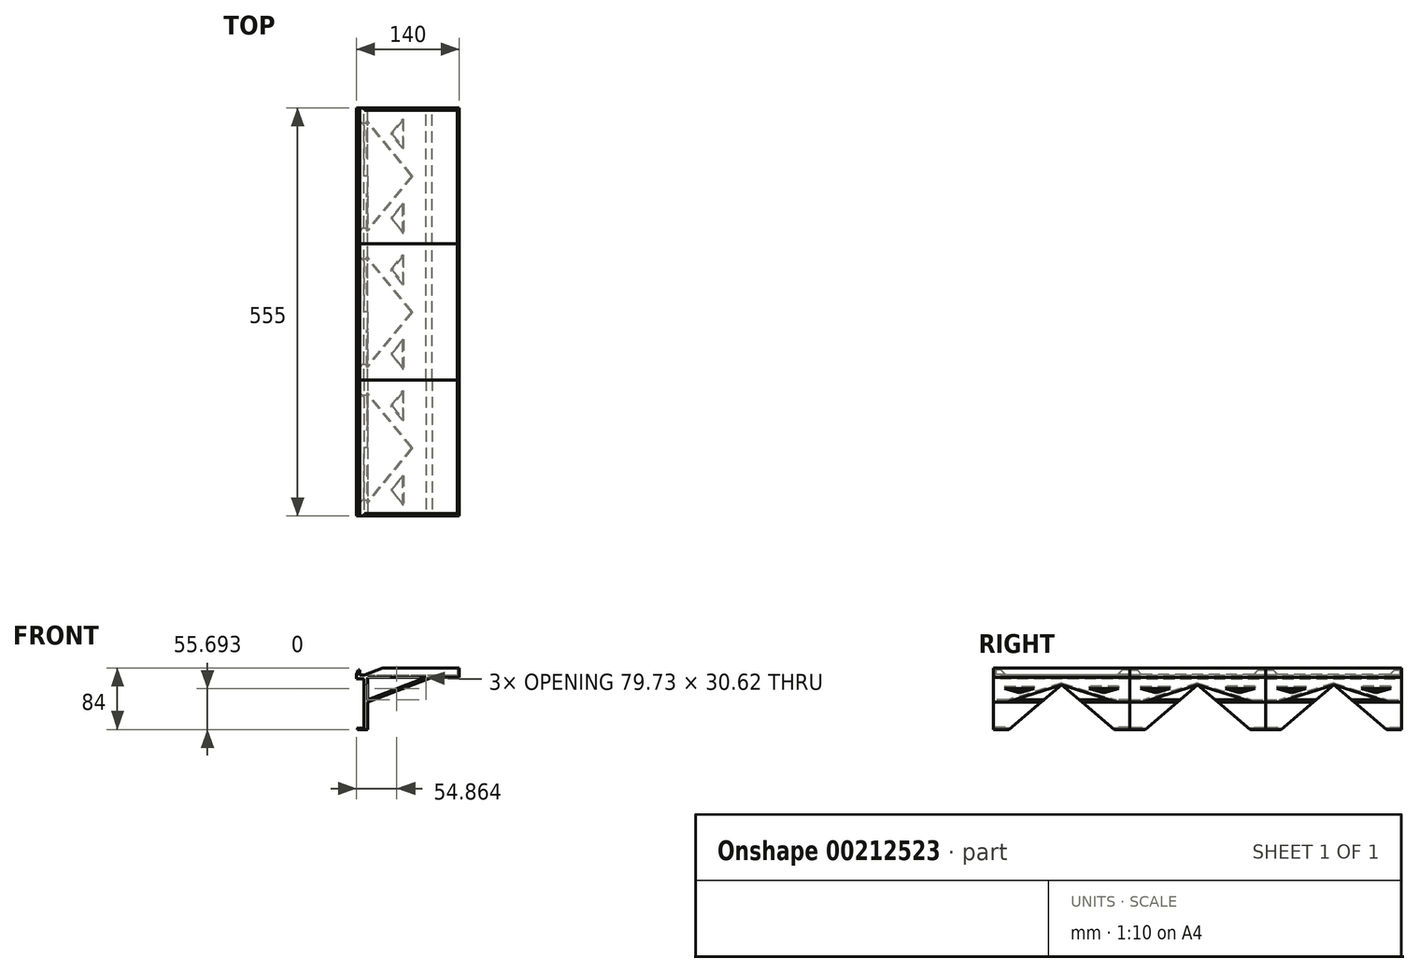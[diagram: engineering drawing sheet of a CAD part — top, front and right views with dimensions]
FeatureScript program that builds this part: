
annotation { "Feature Type Name" : "Feature", "Feature Type Description" : "" }
export const myFeature = defineFeature(function(context is Context, id is Id, definition is map)
    precondition{}
    {
        {
            var Q0;
            Q0=qCreatedBy(makeId("Front.planeOp"),FACE);
            var sketch = newSketch(context, id + "F0", { "sketchPlane" : qUnion([Q0])});
            skLineSegment(sketch, "E0", {"start": v(4.72, -35.17) * mm, "end": v(4.72, 31.83) * mm});
            skLineSegment(sketch, "E1", {"start": v(4.72, 31.83) * mm, "end": v(-5.28, 31.83) * mm});
            skLineSegment(sketch, "E2", {"start": v(-5.28, 31.83) * mm, "end": v(-5.28, 37.83) * mm});
            skLineSegment(sketch, "E3", {"start": v(-3.03, 43.83) * mm, "end": v(-0.78, 43.83) * mm});
            skLineSegment(sketch, "E4", {"start": v(-0.78, 43.83) * mm, "end": v(-0.78, 36.83) * mm});
            skLineSegment(sketch, "E5", {"start": v(-0.78, 36.83) * mm, "end": v(9.72, 36.83) * mm});
            skLineSegment(sketch, "E6", {"start": v(9.72, 33.83) * mm, "end": v(9.72, 3.21) * mm});
            skLineSegment(sketch, "E7", {"start": v(9.72, -37.17) * mm, "end": v(-3.78, -37.17) * mm});
            skLineSegment(sketch, "E8", {"start": v(-3.78, -37.17) * mm, "end": v(-3.78, -35.17) * mm});
            skLineSegment(sketch, "E9", {"start": v(-0.78, -35.17) * mm, "end": v(4.72, -35.17) * mm});
            skLineSegment(sketch, "E10", {"start": v(9.72, 36.83) * mm, "end": v(131.72, 36.83) * mm});
            skLineSegment(sketch, "E11", {"start": v(134.72, 36.83) * mm, "end": v(134.72, 33.83) * mm});
            skLineSegment(sketch, "E12", {"start": v(134.72, 33.83) * mm, "end": v(97.82, 33.83) * mm});
            skLineSegment(sketch, "E13", {"start": v(-3.03, 43.83) * mm, "end": v(-5.28, 37.83) * mm});
            skPoint(sketch, "E14.orphan", {"position": v(-5.28, 43.83) * mm});
            skLineSegment(sketch, "E15", {"start": v(-0.78, -35.17) * mm, "end": v(-2.28, -34.42) * mm});
            skLineSegment(sketch, "E16", {"start": v(-2.28, -34.42) * mm, "end": v(-3.78, -35.17) * mm});
            skLineSegment(sketch, "E17", {"start": v(134.72, 36.83) * mm, "end": v(134.72, 46.83) * mm});
            skLineSegment(sketch, "E18", {"start": v(134.72, 46.83) * mm, "end": v(131.72, 46.83) * mm});
            skLineSegment(sketch, "E19", {"start": v(131.72, 46.83) * mm, "end": v(131.72, 36.83) * mm});
            skLineSegment(sketch, "E20", {"start": v(9.72, 0) * mm, "end": v(97.82, 33.83) * mm});
            skLineSegment(sketch, "E21.0", {"start": v(9.72, 3.21) * mm, "end": v(89.45, 33.83) * mm});
            skLineSegment(sketch, "E22.trimOffspring", {"start": v(9.72, 0) * mm, "end": v(9.72, -37.17) * mm});
            skLineSegment(sketch, "E23.trimOffspring", {"start": v(89.45, 33.83) * mm, "end": v(9.72, 33.83) * mm});
            skSolve(sketch);
        }
        {
            var Q0;
            Q0=makeQuery(id+"F0.imprint","IMPRINT",FACE,{"disambiguationData":[TD([[makeQuery(id+"F0.imprint","IMPRINT",EDGE,{"derivedFrom":sQuery(id+"F0.wireOp",EDGE,"E0")}),-1.0]])]});
            extrude(context, id + "F1", {"entities" : qUnion([Q0]), "endBound" : BoundingType.SYMMETRIC, "depth" : 185 * mm, "offsetDistance" : 25 * mm});
        }
        {
            var Q0;
            Q0=makeQuery(id+"F1.opExtrude","SWEPT_FACE",FACE,{"disambiguationData":[OSD([sQuery(id+"F0.wireOp",EDGE,"E4")])]});
            var sketch = newSketch(context, id + "F2", { "sketchPlane" : qUnion([Q0])});
            skLineSegment(sketch, "E24", {"start": v(-92.5, 43.83) * mm, "end": v(-82.5, 43.83) * mm, "construction": true});
            skLineSegment(sketch, "E25", {"start": v(-82.5, 43.83) * mm, "end": v(-76.17, 37.5) * mm});
            skLineSegment(sketch, "E26.MirrorCS", {"start": v(82.5, 43.83) * mm, "end": v(76.17, 37.5) * mm});
            skLineSegment(sketch, "E27", {"start": v(-76.17, 37.5) * mm, "end": v(76.17, 37.5) * mm});
            skLineSegment(sketch, "E28", {"start": v(-82.5, 43.83) * mm, "end": v(82.5, 43.83) * mm});
            skSolve(sketch);
        }
        {
            var Q0;
            Q0=makeQuery(id+"F2.imprint","IMPRINT",FACE,{"disambiguationData":[TD([[makeQuery(id+"F2.imprint","IMPRINT",EDGE,{"derivedFrom":sQuery(id+"F2.wireOp",EDGE,"E25")}),1.0]])]});
            extrude(context, id + "F3", {"entities" : qUnion([Q0]), "operationType" : NewBodyOperationType.REMOVE, "endBound" : BoundingType.THROUGH_ALL, "oppositeDirection" : true, "depth" : 25 * mm, "offsetDistance" : 25 * mm});
        }
        {
            var Q0;
            Q0=qCreatedBy(makeId("Front.planeOp"),FACE);
            cPlane(context, id + "F4", {"entities" : qUnion([Q0]), "cplaneType" : CPlaneType.OFFSET, "offset" : 92.5 * mm, "width" : 150 * mm, "height" : 150 * mm});
        }
        {
            var Q0;
            Q0=makeQuery(id+"F1.opExtrude","SWEPT_FACE",FACE,{"disambiguationData":[OSD([sQuery(id+"F0.wireOp",EDGE,"E0")])]});
            var sketch = newSketch(context, id + "F5", { "sketchPlane" : qUnion([Q0])});
            skLineSegment(sketch, "E29", {"start": v(-86.31, -49.69) * mm, "end": v(0, 23.55) * mm});
            skPoint(sketch, "E29.endSnap0", {"position": v(0, 31.83) * mm});
            skLineSegment(sketch, "E30.MirrorCS", {"start": v(86.31, -49.69) * mm, "end": v(0, 23.55) * mm});
            skLineSegment(sketch, "E31", {"start": v(-86.31, -49.69) * mm, "end": v(86.31, -49.69) * mm});
            skLineSegment(sketch, "E32.MirrorCS", {"start": v(98.69, -49.69) * mm, "end": v(185, 23.55) * mm});
            skLineSegment(sketch, "E33.MirrorCS", {"start": v(271.31, -49.69) * mm, "end": v(185, 23.55) * mm});
            skLineSegment(sketch, "E34.MirrorCS", {"start": v(271.31, -49.69) * mm, "end": v(98.69, -49.69) * mm});
            skLineSegment(sketch, "E35.MirrorCS", {"start": v(-98.69, -49.69) * mm, "end": v(-185, 23.55) * mm});
            skLineSegment(sketch, "E36.MirrorCS", {"start": v(-271.31, -49.69) * mm, "end": v(-185, 23.55) * mm});
            skLineSegment(sketch, "E37.MirrorCS", {"start": v(-271.31, -49.69) * mm, "end": v(-98.69, -49.69) * mm});
            skSolve(sketch);
        }
        {
            var Q0;
            Q0=makeQuery(id+"F5.imprint","IMPRINT",FACE,{"disambiguationData":[TD([[makeQuery(id+"F5.imprint","IMPRINT",EDGE,{"derivedFrom":sQuery(id+"F5.wireOp",EDGE,"E35.MirrorCS")}),1.0]])]});
            var Q1;
            {var subQ0=sQuery(id+"F5.wireOp",EDGE,"E30.MirrorCS");var subQ1=sQuery(id+"F5.wireOp",EDGE,"E29");var subQ2=makeQuery(id+"F5.imprint","INTERSECT",VERTEX,{"derivedFrom":[subQ1,subQ0]});Q1=makeQuery(id+"F5.imprint","IMPRINT",FACE,{"disambiguationData":[TD([[makeQuery(id+"F5.imprint","IMPRINT",EDGE,{"disambiguationData":[TD([[subQ2,1.0]])],"derivedFrom":subQ1}),-1.0]])]});}
            var Q2;
            {var subQ0=sQuery(id+"F5.wireOp",EDGE,"E31");Q2=makeQuery(id+"F5.imprint","IMPRINT",FACE,{"disambiguationData":[TD([[makeQuery(id+"F5.imprint","IMPRINT",EDGE,{"derivedFrom":subQ0}),1.0]])]});}
            var Q3;
            Q3=makeQuery(id+"F5.imprint","IMPRINT",FACE,{"disambiguationData":[TD([[makeQuery(id+"F5.imprint","IMPRINT",EDGE,{"derivedFrom":sQuery(id+"F5.wireOp",EDGE,"E32.MirrorCS")}),-1.0]])]});
            extrude(context, id + "F6", {"entities" : qUnion([Q0, Q1, Q2, Q3]), "operationType" : NewBodyOperationType.REMOVE, "endBound" : BoundingType.THROUGH_ALL, "oppositeDirection" : true, "depth" : 25 * mm, "offsetDistance" : 25 * mm});
        }
        {
            var Q0;
            Q0=makeQuery(id+"F1.opExtrude","SWEPT_FACE",FACE,{"disambiguationData":[OSD([sQuery(id+"F0.wireOp",EDGE,"E0")])]});
            var sketch = newSketch(context, id + "F7", { "sketchPlane" : qUnion([Q0])});
            skLineSegment(sketch, "E38", {"start": v(-67.86, -34.04) * mm, "end": v(-71.94, -37.5) * mm});
            skLineSegment(sketch, "E39", {"start": v(-67.86, -34.04) * mm, "end": v(67.86, -34.04) * mm});
            skLineSegment(sketch, "E40", {"start": v(67.86, -34.04) * mm, "end": v(71.94, -37.5) * mm});
            skLineSegment(sketch, "E41", {"start": v(-71.94, -37.5) * mm, "end": v(71.94, -37.5) * mm});
            skLineSegment(sketch, "E42.MirrorCS", {"start": v(252.86, -34.04) * mm, "end": v(256.94, -37.5) * mm});
            skLineSegment(sketch, "E43.MirrorCS", {"start": v(117.14, -34.04) * mm, "end": v(113.06, -37.5) * mm});
            skLineSegment(sketch, "E44.MirrorCS", {"start": v(256.94, -37.5) * mm, "end": v(113.06, -37.5) * mm});
            skLineSegment(sketch, "E45.MirrorCS", {"start": v(252.86, -34.04) * mm, "end": v(117.14, -34.04) * mm});
            skSolve(sketch);
        }
        {
            var Q0;
            {var subQ32=sQuery(id+"F7.wireOp",EDGE,"E39");Q0=makeQuery(id+"F7.imprint","IMPRINT",FACE,{"disambiguationData":[TD([[makeQuery(id+"F7.imprint","IMPRINT",EDGE,{"derivedFrom":subQ32}),-1.0]])]});}
            var Q1;
            Q1=makeQuery(id+"F7.imprint","IMPRINT",FACE,{"disambiguationData":[TD([[makeQuery(id+"F7.imprint","IMPRINT",EDGE,{"derivedFrom":sQuery(id+"F7.wireOp",EDGE,"E42.MirrorCS")}),-1.0]])]});
            extrude(context, id + "F8", {"entities" : qUnion([Q0, Q1]), "operationType" : NewBodyOperationType.REMOVE, "endBound" : BoundingType.THROUGH_ALL, "depth" : 25 * mm, "offsetDistance" : 25 * mm});
        }
        {
            var Q0;
            Q0=makeQuery(id+"F1.opExtrude","SWEPT_FACE",FACE,{"disambiguationData":[OSD([sQuery(id+"F0.wireOp",EDGE,"E20")])]});
            var sketch = newSketch(context, id + "F9", { "sketchPlane" : qUnion([Q0])});
            skLineSegment(sketch, "E46", {"start": v(74.75, 0) * mm, "end": v(9.07, 74.66) * mm});
            skLineSegment(sketch, "E47.MirrorCS", {"start": v(74.75, 0) * mm, "end": v(9.07, -74.66) * mm});
            skLineSegment(sketch, "E48", {"start": v(9.07, 74.66) * mm, "end": v(9.07, -74.66) * mm});
            skSolve(sketch);
        }
        {
            var Q0;
            {var subQ0=sQuery(id+"F9.wireOp",EDGE,"E46");Q0=makeQuery(id+"F9.imprint","IMPRINT",FACE,{"disambiguationData":[TD([[makeQuery(id+"F9.imprint","IMPRINT",EDGE,{"derivedFrom":subQ0}),1.0]])]});}
            var Q1;
            {var subQ1=makeQuery(id+"F1.opExtrude","SWEPT_FACE",FACE,{"disambiguationData":[OSD([sQuery(id+"F0.wireOp",EDGE,"E20")])]});var subQ2=makeQuery(id+"F6.boolean.opBoolean","INTERSECT",EDGE,{"derivedFrom":[subQ1,makeQuery(id+"F6.opExtrude","SWEPT_FACE",FACE,{"disambiguationData":[OSD([sQuery(id+"F5.wireOp",EDGE,"E29")])]})]});Q1=makeQuery(id+"F9.imprint","IMPRINT",FACE,{"disambiguationData":[TD([[makeQuery(id+"F9.imprint","IMPRINT",EDGE,{"derivedFrom":subQ2}),1.0]])]});}
            var Q2;
            {var subQ0=sQuery(id+"F9.wireOp",EDGE,"E47.MirrorCS");Q2=makeQuery(id+"F9.imprint","IMPRINT",FACE,{"disambiguationData":[TD([[makeQuery(id+"F9.imprint","IMPRINT",EDGE,{"derivedFrom":subQ0}),-1.0]])]});}
            extrude(context, id + "F10", {"entities" : qUnion([Q0, Q1, Q2]), "operationType" : NewBodyOperationType.REMOVE, "oppositeDirection" : true, "depth" : 3 * mm, "offsetDistance" : 25 * mm});
        }
        {
            var Q0;
            Q0=makeQuery(id+"F1.opExtrude","SWEPT_BODY",BODY,{"disambiguationData":[OSD([sQuery(id+"F0.wireOp",EDGE,"E0"),sQuery(id+"F0.wireOp",EDGE,"E1"),sQuery(id+"F0.wireOp",EDGE,"E2"),sQuery(id+"F0.wireOp",EDGE,"E3"),sQuery(id+"F0.wireOp",EDGE,"E4"),sQuery(id+"F0.wireOp",EDGE,"E5"),sQuery(id+"F0.wireOp",EDGE,"E6"),sQuery(id+"F0.wireOp",EDGE,"E7"),sQuery(id+"F0.wireOp",EDGE,"E8"),sQuery(id+"F0.wireOp",EDGE,"E9"),sQuery(id+"F0.wireOp",EDGE,"E10"),sQuery(id+"F0.wireOp",EDGE,"E11"),sQuery(id+"F0.wireOp",EDGE,"E12"),sQuery(id+"F0.wireOp",EDGE,"E13"),sQuery(id+"F0.wireOp",EDGE,"E15"),sQuery(id+"F0.wireOp",EDGE,"E16"),sQuery(id+"F0.wireOp",EDGE,"E17"),sQuery(id+"F0.wireOp",EDGE,"E18"),sQuery(id+"F0.wireOp",EDGE,"E19"),sQuery(id+"F0.wireOp",EDGE,"E20"),sQuery(id+"F0.wireOp",EDGE,"E21.0"),sQuery(id+"F0.wireOp",EDGE,"E22.trimOffspring"),sQuery(id+"F0.wireOp",EDGE,"E23.trimOffspring")])]});
            var Q1;
            Q1=qCreatedBy(id+"F4.planeOp",FACE);
            mirror(context, id + "F11", {"entities" : qUnion([Q0]), "mirrorPlane" : qUnion([Q1])});
        }
        {
            var Q0;
            Q0=makeQuery(id+"F11.opPattern","COPY",FACE,{"derivedFrom":makeQuery(id+"F1.opExtrude","CAP_FACE",FACE,{"disambiguationData":[OSD([sQuery(id+"F0.wireOp",EDGE,"E0"),sQuery(id+"F0.wireOp",EDGE,"E1"),sQuery(id+"F0.wireOp",EDGE,"E2"),sQuery(id+"F0.wireOp",EDGE,"E3"),sQuery(id+"F0.wireOp",EDGE,"E4"),sQuery(id+"F0.wireOp",EDGE,"E5"),sQuery(id+"F0.wireOp",EDGE,"E6"),sQuery(id+"F0.wireOp",EDGE,"E7"),sQuery(id+"F0.wireOp",EDGE,"E8"),sQuery(id+"F0.wireOp",EDGE,"E9"),sQuery(id+"F0.wireOp",EDGE,"E10"),sQuery(id+"F0.wireOp",EDGE,"E11"),sQuery(id+"F0.wireOp",EDGE,"E12"),sQuery(id+"F0.wireOp",EDGE,"E13"),sQuery(id+"F0.wireOp",EDGE,"E15"),sQuery(id+"F0.wireOp",EDGE,"E16"),sQuery(id+"F0.wireOp",EDGE,"E17"),sQuery(id+"F0.wireOp",EDGE,"E18"),sQuery(id+"F0.wireOp",EDGE,"E19"),sQuery(id+"F0.wireOp",EDGE,"E20"),sQuery(id+"F0.wireOp",EDGE,"E21.0"),sQuery(id+"F0.wireOp",EDGE,"E22.trimOffspring"),sQuery(id+"F0.wireOp",EDGE,"E23.trimOffspring")])],"isStart":true}),"instanceName":"1"});
            var sketch = newSketch(context, id + "F12", { "sketchPlane" : qUnion([Q0])});
            skLineSegment(sketch, "E49", {"start": v(5.8, 36.83) * mm, "end": v(131.72, 36.83) * mm});
            skLineSegment(sketch, "E50", {"start": v(131.72, 36.83) * mm, "end": v(131.72, 46.83) * mm});
            skLineSegment(sketch, "E51", {"start": v(131.72, 46.83) * mm, "end": v(24.2, 46.83) * mm});
            skLineSegment(sketch, "E52", {"start": v(24.2, 46.83) * mm, "end": v(5.8, 36.83) * mm});
            skSolve(sketch);
        }
        {
            var Q0;
            Q0=makeQuery(id+"F12.imprint","IMPRINT",FACE,{"disambiguationData":[TD([[makeQuery(id+"F12.imprint","IMPRINT",EDGE,{"derivedFrom":sQuery(id+"F12.wireOp",EDGE,"E49")}),1.0]])]});
            extrude(context, id + "F13", {"entities" : qUnion([Q0]), "operationType" : NewBodyOperationType.ADD, "oppositeDirection" : true, "depth" : 3 * mm, "offsetDistance" : 25 * mm});
        }
        {
            var Q0;
            Q0=makeQuery(id+"F11.opPattern","COPY",BODY,{"derivedFrom":makeQuery(id+"F1.opExtrude","SWEPT_BODY",BODY,{"disambiguationData":[OSD([sQuery(id+"F0.wireOp",EDGE,"E0"),sQuery(id+"F0.wireOp",EDGE,"E1"),sQuery(id+"F0.wireOp",EDGE,"E2"),sQuery(id+"F0.wireOp",EDGE,"E3"),sQuery(id+"F0.wireOp",EDGE,"E4"),sQuery(id+"F0.wireOp",EDGE,"E5"),sQuery(id+"F0.wireOp",EDGE,"E6"),sQuery(id+"F0.wireOp",EDGE,"E7"),sQuery(id+"F0.wireOp",EDGE,"E8"),sQuery(id+"F0.wireOp",EDGE,"E9"),sQuery(id+"F0.wireOp",EDGE,"E10"),sQuery(id+"F0.wireOp",EDGE,"E11"),sQuery(id+"F0.wireOp",EDGE,"E12"),sQuery(id+"F0.wireOp",EDGE,"E13"),sQuery(id+"F0.wireOp",EDGE,"E15"),sQuery(id+"F0.wireOp",EDGE,"E16"),sQuery(id+"F0.wireOp",EDGE,"E17"),sQuery(id+"F0.wireOp",EDGE,"E18"),sQuery(id+"F0.wireOp",EDGE,"E19"),sQuery(id+"F0.wireOp",EDGE,"E20"),sQuery(id+"F0.wireOp",EDGE,"E21.0"),sQuery(id+"F0.wireOp",EDGE,"E22.trimOffspring"),sQuery(id+"F0.wireOp",EDGE,"E23.trimOffspring")])]}),"instanceName":"1"});
            var Q1;
            Q1=qCreatedBy(makeId("Front.planeOp"),FACE);
            mirror(context, id + "F14", {"entities" : qUnion([Q0]), "mirrorPlane" : qUnion([Q1])});
        }
        {
            var Q0;
            {var subQ2=sQuery(id+"F0.wireOp",EDGE,"E7");Q0=makeQuery(id+"F8.boolean.opBoolean","SPLIT",FACE,{"disambiguationData":[TD([makeQuery(id+"F6.boolean.opBoolean","COPY",FACE,{"derivedFrom":makeQuery(id+"F6.opExtrude","SWEPT_FACE",FACE,{"disambiguationData":[OSD([sQuery(id+"F5.wireOp",EDGE,"E30.MirrorCS")])]})})])],"derivedFrom":makeQuery(id+"F1.opExtrude","SWEPT_FACE",FACE,{"disambiguationData":[OSD([subQ2])]})});}
            var sketch = newSketch(context, id + "F15", { "sketchPlane" : qUnion([Q0])});
            skLineSegment(sketch, "E53", {"start": v(4.66, 69.27) * mm, "end": v(-3.78, 78.71) * mm});
            skLineSegment(sketch, "E54", {"start": v(-3.78, 78.71) * mm, "end": v(-3.78, 67.84) * mm});
            skLineSegment(sketch, "E55", {"start": v(-3.78, 67.84) * mm, "end": v(4.66, 69.27) * mm});
            skLineSegment(sketch, "E56.MirrorCS", {"start": v(4.66, -69.27) * mm, "end": v(-3.78, -78.71) * mm});
            skLineSegment(sketch, "E57.MirrorCS", {"start": v(-3.78, -78.71) * mm, "end": v(-3.78, -67.84) * mm});
            skLineSegment(sketch, "E58.MirrorCS", {"start": v(-3.78, -67.84) * mm, "end": v(4.66, -69.27) * mm});
            skSolve(sketch);
        }
        {
            var Q0;
            {var subQ0=sQuery(id+"F15.wireOp",EDGE,"E55");Q0=makeQuery(id+"F15.imprint","IMPRINT",FACE,{"disambiguationData":[TD([[makeQuery(id+"F15.imprint","IMPRINT",EDGE,{"derivedFrom":subQ0}),1.0]])]});}
            var Q1;
            {var subQ0=sQuery(id+"F15.wireOp",EDGE,"E54");var subQ3=sQuery(id+"F0.wireOp",EDGE,"E7");var subQ4=makeQuery(id+"F1.opExtrude","SWEPT_FACE",FACE,{"disambiguationData":[OSD([subQ3])]});var subQ5=makeQuery(id+"F8.opExtrude","SWEPT_FACE",FACE,{"disambiguationData":[OSD([sQuery(id+"F7.wireOp",EDGE,"E40")])]});var subQ7=makeQuery(id+"F8.boolean.opBoolean","INTERSECT",EDGE,{"derivedFrom":[subQ4,subQ5]});var subQ9=makeQuery(id+"F15.imprint","INTERSECT",VERTEX,{"derivedFrom":[subQ7,subQ0]});Q1=makeQuery(id+"F15.imprint","IMPRINT",FACE,{"disambiguationData":[TD([[makeQuery(id+"F15.imprint","IMPRINT",EDGE,{"disambiguationData":[TD([[subQ9,1.0]])],"derivedFrom":subQ7}),-1.0]])]});}
            var Q2;
            Q2=makeQuery(id+"F15.imprint","IMPRINT",FACE,{"disambiguationData":[TD([[makeQuery(id+"F15.imprint","IMPRINT",EDGE,{"derivedFrom":sQuery(id+"F15.wireOp",EDGE,"E56.MirrorCS")}),-1.0]])]});
            extrude(context, id + "F16", {"entities" : qUnion([Q0, Q1, Q2]), "operationType" : NewBodyOperationType.REMOVE, "oppositeDirection" : true, "depth" : 6 * mm, "offsetDistance" : 25 * mm});
        }
        {
            var Q0;
            Q0=makeQuery(id+"F14.opPattern","COPY",BODY,{"derivedFrom":makeQuery(id+"F11.opPattern","COPY",BODY,{"derivedFrom":makeQuery(id+"F1.opExtrude","SWEPT_BODY",BODY,{"disambiguationData":[OSD([sQuery(id+"F0.wireOp",EDGE,"E0"),sQuery(id+"F0.wireOp",EDGE,"E1"),sQuery(id+"F0.wireOp",EDGE,"E2"),sQuery(id+"F0.wireOp",EDGE,"E3"),sQuery(id+"F0.wireOp",EDGE,"E4"),sQuery(id+"F0.wireOp",EDGE,"E5"),sQuery(id+"F0.wireOp",EDGE,"E6"),sQuery(id+"F0.wireOp",EDGE,"E7"),sQuery(id+"F0.wireOp",EDGE,"E8"),sQuery(id+"F0.wireOp",EDGE,"E9"),sQuery(id+"F0.wireOp",EDGE,"E10"),sQuery(id+"F0.wireOp",EDGE,"E11"),sQuery(id+"F0.wireOp",EDGE,"E12"),sQuery(id+"F0.wireOp",EDGE,"E13"),sQuery(id+"F0.wireOp",EDGE,"E15"),sQuery(id+"F0.wireOp",EDGE,"E16"),sQuery(id+"F0.wireOp",EDGE,"E17"),sQuery(id+"F0.wireOp",EDGE,"E18"),sQuery(id+"F0.wireOp",EDGE,"E19"),sQuery(id+"F0.wireOp",EDGE,"E20"),sQuery(id+"F0.wireOp",EDGE,"E21.0"),sQuery(id+"F0.wireOp",EDGE,"E22.trimOffspring"),sQuery(id+"F0.wireOp",EDGE,"E23.trimOffspring")])]}),"instanceName":"1"}),"instanceName":"1"});
            deleteBodies(context, id + "F17", {"entities" : qUnion([Q0])});
        }
        {
            var Q0;
            Q0=makeQuery(id+"F11.opPattern","COPY",BODY,{"derivedFrom":makeQuery(id+"F1.opExtrude","SWEPT_BODY",BODY,{"disambiguationData":[OSD([sQuery(id+"F0.wireOp",EDGE,"E0"),sQuery(id+"F0.wireOp",EDGE,"E1"),sQuery(id+"F0.wireOp",EDGE,"E2"),sQuery(id+"F0.wireOp",EDGE,"E3"),sQuery(id+"F0.wireOp",EDGE,"E4"),sQuery(id+"F0.wireOp",EDGE,"E5"),sQuery(id+"F0.wireOp",EDGE,"E6"),sQuery(id+"F0.wireOp",EDGE,"E7"),sQuery(id+"F0.wireOp",EDGE,"E8"),sQuery(id+"F0.wireOp",EDGE,"E9"),sQuery(id+"F0.wireOp",EDGE,"E10"),sQuery(id+"F0.wireOp",EDGE,"E11"),sQuery(id+"F0.wireOp",EDGE,"E12"),sQuery(id+"F0.wireOp",EDGE,"E13"),sQuery(id+"F0.wireOp",EDGE,"E15"),sQuery(id+"F0.wireOp",EDGE,"E16"),sQuery(id+"F0.wireOp",EDGE,"E17"),sQuery(id+"F0.wireOp",EDGE,"E18"),sQuery(id+"F0.wireOp",EDGE,"E19"),sQuery(id+"F0.wireOp",EDGE,"E20"),sQuery(id+"F0.wireOp",EDGE,"E21.0"),sQuery(id+"F0.wireOp",EDGE,"E22.trimOffspring"),sQuery(id+"F0.wireOp",EDGE,"E23.trimOffspring")])]}),"instanceName":"1"});
            deleteBodies(context, id + "F18", {"entities" : qUnion([Q0])});
        }
        {
            var Q0;
            Q0=makeQuery(id+"F1.opExtrude","SWEPT_BODY",BODY,{"disambiguationData":[OSD([sQuery(id+"F0.wireOp",EDGE,"E0"),sQuery(id+"F0.wireOp",EDGE,"E1"),sQuery(id+"F0.wireOp",EDGE,"E2"),sQuery(id+"F0.wireOp",EDGE,"E3"),sQuery(id+"F0.wireOp",EDGE,"E4"),sQuery(id+"F0.wireOp",EDGE,"E5"),sQuery(id+"F0.wireOp",EDGE,"E6"),sQuery(id+"F0.wireOp",EDGE,"E7"),sQuery(id+"F0.wireOp",EDGE,"E8"),sQuery(id+"F0.wireOp",EDGE,"E9"),sQuery(id+"F0.wireOp",EDGE,"E10"),sQuery(id+"F0.wireOp",EDGE,"E11"),sQuery(id+"F0.wireOp",EDGE,"E12"),sQuery(id+"F0.wireOp",EDGE,"E13"),sQuery(id+"F0.wireOp",EDGE,"E15"),sQuery(id+"F0.wireOp",EDGE,"E16"),sQuery(id+"F0.wireOp",EDGE,"E17"),sQuery(id+"F0.wireOp",EDGE,"E18"),sQuery(id+"F0.wireOp",EDGE,"E19"),sQuery(id+"F0.wireOp",EDGE,"E20"),sQuery(id+"F0.wireOp",EDGE,"E21.0"),sQuery(id+"F0.wireOp",EDGE,"E22.trimOffspring"),sQuery(id+"F0.wireOp",EDGE,"E23.trimOffspring")])]});
            var Q1;
            Q1=qCreatedBy(id+"F4.planeOp",FACE);
            mirror(context, id + "F19", {"entities" : qUnion([Q0]), "mirrorPlane" : qUnion([Q1])});
        }
        {
            var Q0;
            Q0=makeQuery(id+"F19.opPattern","COPY",BODY,{"derivedFrom":makeQuery(id+"F1.opExtrude","SWEPT_BODY",BODY,{"disambiguationData":[OSD([sQuery(id+"F0.wireOp",EDGE,"E0"),sQuery(id+"F0.wireOp",EDGE,"E1"),sQuery(id+"F0.wireOp",EDGE,"E2"),sQuery(id+"F0.wireOp",EDGE,"E3"),sQuery(id+"F0.wireOp",EDGE,"E4"),sQuery(id+"F0.wireOp",EDGE,"E5"),sQuery(id+"F0.wireOp",EDGE,"E6"),sQuery(id+"F0.wireOp",EDGE,"E7"),sQuery(id+"F0.wireOp",EDGE,"E8"),sQuery(id+"F0.wireOp",EDGE,"E9"),sQuery(id+"F0.wireOp",EDGE,"E10"),sQuery(id+"F0.wireOp",EDGE,"E11"),sQuery(id+"F0.wireOp",EDGE,"E12"),sQuery(id+"F0.wireOp",EDGE,"E13"),sQuery(id+"F0.wireOp",EDGE,"E15"),sQuery(id+"F0.wireOp",EDGE,"E16"),sQuery(id+"F0.wireOp",EDGE,"E17"),sQuery(id+"F0.wireOp",EDGE,"E18"),sQuery(id+"F0.wireOp",EDGE,"E19"),sQuery(id+"F0.wireOp",EDGE,"E20"),sQuery(id+"F0.wireOp",EDGE,"E21.0"),sQuery(id+"F0.wireOp",EDGE,"E22.trimOffspring"),sQuery(id+"F0.wireOp",EDGE,"E23.trimOffspring")])]}),"instanceName":"1"});
            var Q1;
            Q1=qCreatedBy(makeId("Front.planeOp"),FACE);
            mirror(context, id + "F20", {"entities" : qUnion([Q0]), "mirrorPlane" : qUnion([Q1])});
        }
        {
            var Q0;
            Q0=makeQuery(id+"F1.opExtrude","SWEPT_FACE",FACE,{"disambiguationData":[OSD([sQuery(id+"F0.wireOp",EDGE,"E20")])]});
            var sketch = newSketch(context, id + "F21", { "sketchPlane" : qUnion([Q0])});
            skLineSegment(sketch, "E59", {"start": v(41.91, 37.33) * mm, "end": v(53.18, 47.24) * mm, "construction": true});
            skLineSegment(sketch, "E60", {"start": v(56.26, 92.5) * mm, "end": v(56.26, 77.5) * mm, "construction": true});
            skLineSegment(sketch, "E61", {"start": v(56.26, 77.5) * mm, "end": v(9.07, 77.5) * mm, "construction": true});
            skLineSegment(sketch, "E62", {"start": v(61.62, 37.64) * mm, "end": v(61.62, 77.5) * mm});
            skLineSegment(sketch, "E63", {"start": v(56.26, 77.5) * mm, "end": v(61.62, 77.5) * mm});
            skLineSegment(sketch, "E64", {"start": v(44.53, 57.07) * mm, "end": v(61.62, 37.64) * mm});
            skPoint(sketch, "E65.orphan", {"position": v(61.62, 92.5) * mm});
            skLineSegment(sketch, "E66", {"start": v(61.62, 77.5) * mm, "end": v(44.53, 57.07) * mm});
            skPoint(sketch, "E67.orphan", {"position": v(-3.2, 0) * mm});
            skLineSegment(sketch, "E68.MirrorCS", {"start": v(56.26, -77.5) * mm, "end": v(61.62, -77.5) * mm});
            skLineSegment(sketch, "E69.MirrorCS", {"start": v(61.62, -77.5) * mm, "end": v(44.53, -57.07) * mm});
            skLineSegment(sketch, "E70.MirrorCS", {"start": v(61.62, -37.64) * mm, "end": v(61.62, -77.5) * mm});
            skLineSegment(sketch, "E71.MirrorCS", {"start": v(41.91, -37.33) * mm, "end": v(53.18, -47.24) * mm, "construction": true});
            skLineSegment(sketch, "E72.MirrorCS", {"start": v(44.53, -57.07) * mm, "end": v(61.62, -37.64) * mm});
            skSolve(sketch);
        }
        {
            var Q0;
            Q0=makeQuery(id+"F21.imprint","IMPRINT",FACE,{"disambiguationData":[TD([[makeQuery(id+"F21.imprint","IMPRINT",EDGE,{"derivedFrom":sQuery(id+"F21.wireOp",EDGE,"E62")}),1.0]])]});
            var Q1;
            Q1=makeQuery(id+"F21.imprint","IMPRINT",FACE,{"disambiguationData":[TD([[makeQuery(id+"F21.imprint","IMPRINT",EDGE,{"derivedFrom":sQuery(id+"F21.wireOp",EDGE,"E69.MirrorCS")}),-1.0]])]});
            var Q2;
            Q2=makeQuery(id+"F21.imprint","IMPRINT",FACE,{"disambiguationData":[TD([[makeQuery(id+"F21.imprint","IMPRINT",EDGE,{"derivedFrom":sQuery(id+"F21.wireOp",EDGE,"E69.MirrorCS")}),-1.0]])]});
            extrude(context, id + "F22", {"entities" : qUnion([Q0, Q1, Q2]), "operationType" : NewBodyOperationType.REMOVE, "oppositeDirection" : true, "depth" : 10 * mm, "offsetDistance" : 25 * mm});
        }
        {
            var Q0;
            Q0=makeQuery(id+"F19.opPattern","COPY",BODY,{"derivedFrom":makeQuery(id+"F1.opExtrude","SWEPT_BODY",BODY,{"disambiguationData":[OSD([sQuery(id+"F0.wireOp",EDGE,"E0"),sQuery(id+"F0.wireOp",EDGE,"E1"),sQuery(id+"F0.wireOp",EDGE,"E2"),sQuery(id+"F0.wireOp",EDGE,"E3"),sQuery(id+"F0.wireOp",EDGE,"E4"),sQuery(id+"F0.wireOp",EDGE,"E5"),sQuery(id+"F0.wireOp",EDGE,"E6"),sQuery(id+"F0.wireOp",EDGE,"E7"),sQuery(id+"F0.wireOp",EDGE,"E8"),sQuery(id+"F0.wireOp",EDGE,"E9"),sQuery(id+"F0.wireOp",EDGE,"E10"),sQuery(id+"F0.wireOp",EDGE,"E11"),sQuery(id+"F0.wireOp",EDGE,"E12"),sQuery(id+"F0.wireOp",EDGE,"E13"),sQuery(id+"F0.wireOp",EDGE,"E15"),sQuery(id+"F0.wireOp",EDGE,"E16"),sQuery(id+"F0.wireOp",EDGE,"E17"),sQuery(id+"F0.wireOp",EDGE,"E18"),sQuery(id+"F0.wireOp",EDGE,"E19"),sQuery(id+"F0.wireOp",EDGE,"E20"),sQuery(id+"F0.wireOp",EDGE,"E21.0"),sQuery(id+"F0.wireOp",EDGE,"E22.trimOffspring"),sQuery(id+"F0.wireOp",EDGE,"E23.trimOffspring")])]}),"instanceName":"1"});
            deleteBodies(context, id + "F23", {"entities" : qUnion([Q0])});
        }
        {
            var Q0;
            Q0=makeQuery(id+"F20.opPattern","COPY",BODY,{"derivedFrom":makeQuery(id+"F19.opPattern","COPY",BODY,{"derivedFrom":makeQuery(id+"F1.opExtrude","SWEPT_BODY",BODY,{"disambiguationData":[OSD([sQuery(id+"F0.wireOp",EDGE,"E0"),sQuery(id+"F0.wireOp",EDGE,"E1"),sQuery(id+"F0.wireOp",EDGE,"E2"),sQuery(id+"F0.wireOp",EDGE,"E3"),sQuery(id+"F0.wireOp",EDGE,"E4"),sQuery(id+"F0.wireOp",EDGE,"E5"),sQuery(id+"F0.wireOp",EDGE,"E6"),sQuery(id+"F0.wireOp",EDGE,"E7"),sQuery(id+"F0.wireOp",EDGE,"E8"),sQuery(id+"F0.wireOp",EDGE,"E9"),sQuery(id+"F0.wireOp",EDGE,"E10"),sQuery(id+"F0.wireOp",EDGE,"E11"),sQuery(id+"F0.wireOp",EDGE,"E12"),sQuery(id+"F0.wireOp",EDGE,"E13"),sQuery(id+"F0.wireOp",EDGE,"E15"),sQuery(id+"F0.wireOp",EDGE,"E16"),sQuery(id+"F0.wireOp",EDGE,"E17"),sQuery(id+"F0.wireOp",EDGE,"E18"),sQuery(id+"F0.wireOp",EDGE,"E19"),sQuery(id+"F0.wireOp",EDGE,"E20"),sQuery(id+"F0.wireOp",EDGE,"E21.0"),sQuery(id+"F0.wireOp",EDGE,"E22.trimOffspring"),sQuery(id+"F0.wireOp",EDGE,"E23.trimOffspring")])]}),"instanceName":"1"}),"instanceName":"1"});
            deleteBodies(context, id + "F24", {"entities" : qUnion([Q0])});
        }
        {
            var Q0;
            Q0=makeQuery(id+"F1.opExtrude","SWEPT_BODY",BODY,{"disambiguationData":[OSD([sQuery(id+"F0.wireOp",EDGE,"E0"),sQuery(id+"F0.wireOp",EDGE,"E1"),sQuery(id+"F0.wireOp",EDGE,"E2"),sQuery(id+"F0.wireOp",EDGE,"E3"),sQuery(id+"F0.wireOp",EDGE,"E4"),sQuery(id+"F0.wireOp",EDGE,"E5"),sQuery(id+"F0.wireOp",EDGE,"E6"),sQuery(id+"F0.wireOp",EDGE,"E7"),sQuery(id+"F0.wireOp",EDGE,"E8"),sQuery(id+"F0.wireOp",EDGE,"E9"),sQuery(id+"F0.wireOp",EDGE,"E10"),sQuery(id+"F0.wireOp",EDGE,"E11"),sQuery(id+"F0.wireOp",EDGE,"E12"),sQuery(id+"F0.wireOp",EDGE,"E13"),sQuery(id+"F0.wireOp",EDGE,"E15"),sQuery(id+"F0.wireOp",EDGE,"E16"),sQuery(id+"F0.wireOp",EDGE,"E17"),sQuery(id+"F0.wireOp",EDGE,"E18"),sQuery(id+"F0.wireOp",EDGE,"E19"),sQuery(id+"F0.wireOp",EDGE,"E20"),sQuery(id+"F0.wireOp",EDGE,"E21.0"),sQuery(id+"F0.wireOp",EDGE,"E22.trimOffspring"),sQuery(id+"F0.wireOp",EDGE,"E23.trimOffspring")])]});
            var Q1;
            Q1=qCreatedBy(id+"F4.planeOp",FACE);
            mirror(context, id + "F25", {"entities" : qUnion([Q0]), "mirrorPlane" : qUnion([Q1])});
        }
        {
            var Q0;
            Q0=makeQuery(id+"F25.opPattern","COPY",BODY,{"derivedFrom":makeQuery(id+"F1.opExtrude","SWEPT_BODY",BODY,{"disambiguationData":[OSD([sQuery(id+"F0.wireOp",EDGE,"E0"),sQuery(id+"F0.wireOp",EDGE,"E1"),sQuery(id+"F0.wireOp",EDGE,"E2"),sQuery(id+"F0.wireOp",EDGE,"E3"),sQuery(id+"F0.wireOp",EDGE,"E4"),sQuery(id+"F0.wireOp",EDGE,"E5"),sQuery(id+"F0.wireOp",EDGE,"E6"),sQuery(id+"F0.wireOp",EDGE,"E7"),sQuery(id+"F0.wireOp",EDGE,"E8"),sQuery(id+"F0.wireOp",EDGE,"E9"),sQuery(id+"F0.wireOp",EDGE,"E10"),sQuery(id+"F0.wireOp",EDGE,"E11"),sQuery(id+"F0.wireOp",EDGE,"E12"),sQuery(id+"F0.wireOp",EDGE,"E13"),sQuery(id+"F0.wireOp",EDGE,"E15"),sQuery(id+"F0.wireOp",EDGE,"E16"),sQuery(id+"F0.wireOp",EDGE,"E17"),sQuery(id+"F0.wireOp",EDGE,"E18"),sQuery(id+"F0.wireOp",EDGE,"E19"),sQuery(id+"F0.wireOp",EDGE,"E20"),sQuery(id+"F0.wireOp",EDGE,"E21.0"),sQuery(id+"F0.wireOp",EDGE,"E22.trimOffspring"),sQuery(id+"F0.wireOp",EDGE,"E23.trimOffspring")])]}),"instanceName":"1"});
            var Q1;
            Q1=qCreatedBy(makeId("Front.planeOp"),FACE);
            mirror(context, id + "F26", {"entities" : qUnion([Q0]), "mirrorPlane" : qUnion([Q1])});
        }
        {
            var Q0;
            Q0=makeQuery(id+"F26.opPattern","COPY",BODY,{"derivedFrom":makeQuery(id+"F25.opPattern","COPY",BODY,{"derivedFrom":makeQuery(id+"F1.opExtrude","SWEPT_BODY",BODY,{"disambiguationData":[OSD([sQuery(id+"F0.wireOp",EDGE,"E0"),sQuery(id+"F0.wireOp",EDGE,"E1"),sQuery(id+"F0.wireOp",EDGE,"E2"),sQuery(id+"F0.wireOp",EDGE,"E3"),sQuery(id+"F0.wireOp",EDGE,"E4"),sQuery(id+"F0.wireOp",EDGE,"E5"),sQuery(id+"F0.wireOp",EDGE,"E6"),sQuery(id+"F0.wireOp",EDGE,"E7"),sQuery(id+"F0.wireOp",EDGE,"E8"),sQuery(id+"F0.wireOp",EDGE,"E9"),sQuery(id+"F0.wireOp",EDGE,"E10"),sQuery(id+"F0.wireOp",EDGE,"E11"),sQuery(id+"F0.wireOp",EDGE,"E12"),sQuery(id+"F0.wireOp",EDGE,"E13"),sQuery(id+"F0.wireOp",EDGE,"E15"),sQuery(id+"F0.wireOp",EDGE,"E16"),sQuery(id+"F0.wireOp",EDGE,"E17"),sQuery(id+"F0.wireOp",EDGE,"E18"),sQuery(id+"F0.wireOp",EDGE,"E19"),sQuery(id+"F0.wireOp",EDGE,"E20"),sQuery(id+"F0.wireOp",EDGE,"E21.0"),sQuery(id+"F0.wireOp",EDGE,"E22.trimOffspring"),sQuery(id+"F0.wireOp",EDGE,"E23.trimOffspring")])]}),"instanceName":"1"}),"instanceName":"1"});
            deleteBodies(context, id + "F27", {"entities" : qUnion([Q0])});
        }
        {
            var Q0;
            Q0=makeQuery(id+"F25.opPattern","COPY",FACE,{"derivedFrom":makeQuery(id+"F1.opExtrude","CAP_FACE",FACE,{"disambiguationData":[OSD([sQuery(id+"F0.wireOp",EDGE,"E0"),sQuery(id+"F0.wireOp",EDGE,"E1"),sQuery(id+"F0.wireOp",EDGE,"E2"),sQuery(id+"F0.wireOp",EDGE,"E3"),sQuery(id+"F0.wireOp",EDGE,"E4"),sQuery(id+"F0.wireOp",EDGE,"E5"),sQuery(id+"F0.wireOp",EDGE,"E6"),sQuery(id+"F0.wireOp",EDGE,"E7"),sQuery(id+"F0.wireOp",EDGE,"E8"),sQuery(id+"F0.wireOp",EDGE,"E9"),sQuery(id+"F0.wireOp",EDGE,"E10"),sQuery(id+"F0.wireOp",EDGE,"E11"),sQuery(id+"F0.wireOp",EDGE,"E12"),sQuery(id+"F0.wireOp",EDGE,"E13"),sQuery(id+"F0.wireOp",EDGE,"E15"),sQuery(id+"F0.wireOp",EDGE,"E16"),sQuery(id+"F0.wireOp",EDGE,"E17"),sQuery(id+"F0.wireOp",EDGE,"E18"),sQuery(id+"F0.wireOp",EDGE,"E19"),sQuery(id+"F0.wireOp",EDGE,"E20"),sQuery(id+"F0.wireOp",EDGE,"E21.0"),sQuery(id+"F0.wireOp",EDGE,"E22.trimOffspring"),sQuery(id+"F0.wireOp",EDGE,"E23.trimOffspring")])],"isStart":true}),"instanceName":"1"});
            var sketch = newSketch(context, id + "F28", { "sketchPlane" : qUnion([Q0])});
            skLineSegment(sketch, "E73", {"start": v(5.4, 36.83) * mm, "end": v(30.03, 46.83) * mm});
            skLineSegment(sketch, "E74", {"start": v(5.4, 36.83) * mm, "end": v(131.72, 36.83) * mm});
            skLineSegment(sketch, "E75", {"start": v(131.72, 36.83) * mm, "end": v(131.72, 46.83) * mm});
            skLineSegment(sketch, "E76", {"start": v(131.72, 46.83) * mm, "end": v(30.03, 46.83) * mm});
            skPoint(sketch, "E77.orphan", {"position": v(9.72, 46.83) * mm});
            skSolve(sketch);
        }
        {
            var Q0;
            Q0=makeQuery(id+"F28.imprint","IMPRINT",FACE,{"disambiguationData":[TD([[makeQuery(id+"F28.imprint","IMPRINT",EDGE,{"derivedFrom":sQuery(id+"F28.wireOp",EDGE,"E73")}),-1.0]])]});
            extrude(context, id + "F29", {"entities" : qUnion([Q0]), "operationType" : NewBodyOperationType.ADD, "oppositeDirection" : true, "depth" : 3 * mm, "offsetDistance" : 25 * mm});
        }
        {
            var Q0;
            Q0=makeQuery(id+"F25.opPattern","COPY",BODY,{"derivedFrom":makeQuery(id+"F1.opExtrude","SWEPT_BODY",BODY,{"disambiguationData":[OSD([sQuery(id+"F0.wireOp",EDGE,"E0"),sQuery(id+"F0.wireOp",EDGE,"E1"),sQuery(id+"F0.wireOp",EDGE,"E2"),sQuery(id+"F0.wireOp",EDGE,"E3"),sQuery(id+"F0.wireOp",EDGE,"E4"),sQuery(id+"F0.wireOp",EDGE,"E5"),sQuery(id+"F0.wireOp",EDGE,"E6"),sQuery(id+"F0.wireOp",EDGE,"E7"),sQuery(id+"F0.wireOp",EDGE,"E8"),sQuery(id+"F0.wireOp",EDGE,"E9"),sQuery(id+"F0.wireOp",EDGE,"E10"),sQuery(id+"F0.wireOp",EDGE,"E11"),sQuery(id+"F0.wireOp",EDGE,"E12"),sQuery(id+"F0.wireOp",EDGE,"E13"),sQuery(id+"F0.wireOp",EDGE,"E15"),sQuery(id+"F0.wireOp",EDGE,"E16"),sQuery(id+"F0.wireOp",EDGE,"E17"),sQuery(id+"F0.wireOp",EDGE,"E18"),sQuery(id+"F0.wireOp",EDGE,"E19"),sQuery(id+"F0.wireOp",EDGE,"E20"),sQuery(id+"F0.wireOp",EDGE,"E21.0"),sQuery(id+"F0.wireOp",EDGE,"E22.trimOffspring"),sQuery(id+"F0.wireOp",EDGE,"E23.trimOffspring")])]}),"instanceName":"1"});
            var Q1;
            Q1=qCreatedBy(makeId("Front.planeOp"),FACE);
            mirror(context, id + "F30", {"entities" : qUnion([Q0]), "mirrorPlane" : qUnion([Q1])});
        }
    });
